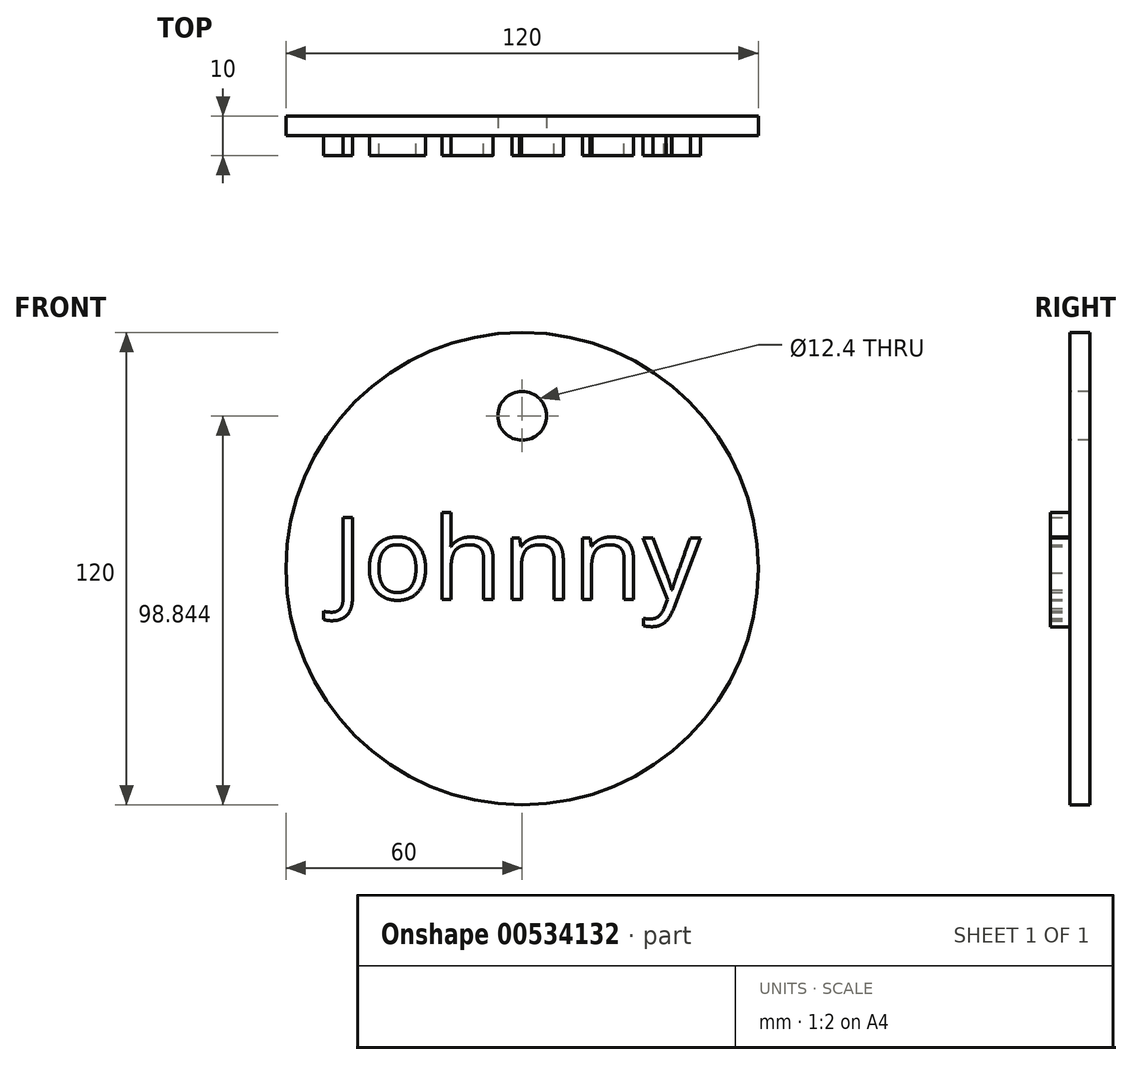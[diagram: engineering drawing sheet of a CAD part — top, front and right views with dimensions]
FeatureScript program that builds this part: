
annotation { "Feature Type Name" : "Feature", "Feature Type Description" : "" }
export const myFeature = defineFeature(function(context is Context, id is Id, definition is map)
    precondition{}
    {
        {
            var Q0;
            Q0=qCreatedBy(makeId("Front.planeOp"),FACE);
            var sketch = newSketch(context, id + "F0", { "sketchPlane" : qUnion([Q0])});
            skCircle(sketch, "E0", {"center": v(0, 0) * mm, "radius": 60 * mm});
            skSolve(sketch);
        }
        {
            var Q0;
            Q0 = qSketchRegion(id + "F0", true);
            extrude(context, id + "F1", {"entities" : qUnion([Q0]), "depth" : 5 * mm, "offsetDistance" : 25 * mm});
        }
        {
            var Q0;
            Q0=makeQuery(id+"F1.opExtrude","CAP_FACE",FACE,{"disambiguationData":[OSD([sQuery(id+"F0.wireOp",EDGE,"E0")])],"isStart":false});
            var sketch = newSketch(context, id + "F2", { "sketchPlane" : qUnion([Q0])});
            skText(sketch, "E1", { "text": "Johnny", "fontName": "OpenSans-Regular.ttf"});
            const initialGuessF2  = {"E1": [-0.04823, -0.00776, 1, 0, 0.02093]};
            skSetInitialGuess(sketch, initialGuessF2);
            skSolve(sketch);
        }
        {
            var Q0;
            Q0 = qSketchRegion(id + "F2", true);
            extrude(context, id + "F3", {"entities" : qUnion([Q0]), "operationType" : NewBodyOperationType.ADD, "depth" : 5 * mm, "offsetDistance" : 25 * mm});
        }
        {
            var Q0;
            {var subQ6=sQuery(id+"F0.wireOp",EDGE,"E0");Q0=makeQuery(id+"F3.boolean.opBoolean","SPLIT",FACE,{"disambiguationData":[TD([makeQuery(id+"F1.opExtrude","SWEPT_FACE",FACE,{"disambiguationData":[OSD([subQ6])]})])],"derivedFrom":makeQuery(id+"F1.opExtrude","CAP_FACE",FACE,{"disambiguationData":[OSD([subQ6])],"isStart":false})});}
            var sketch = newSketch(context, id + "F4", { "sketchPlane" : qUnion([Q0])});
            skCircle(sketch, "E2", {"center": v(0, 38.84) * mm, "radius": 6.2 * mm});
            skSolve(sketch);
        }
        {
            var Q0;
            Q0 = qSketchRegion(id + "F4", true);
            extrude(context, id + "F5", {"entities" : qUnion([Q0]), "operationType" : NewBodyOperationType.REMOVE, "oppositeDirection" : true, "depth" : 10 * mm, "offsetDistance" : 25 * mm});
        }
    });
